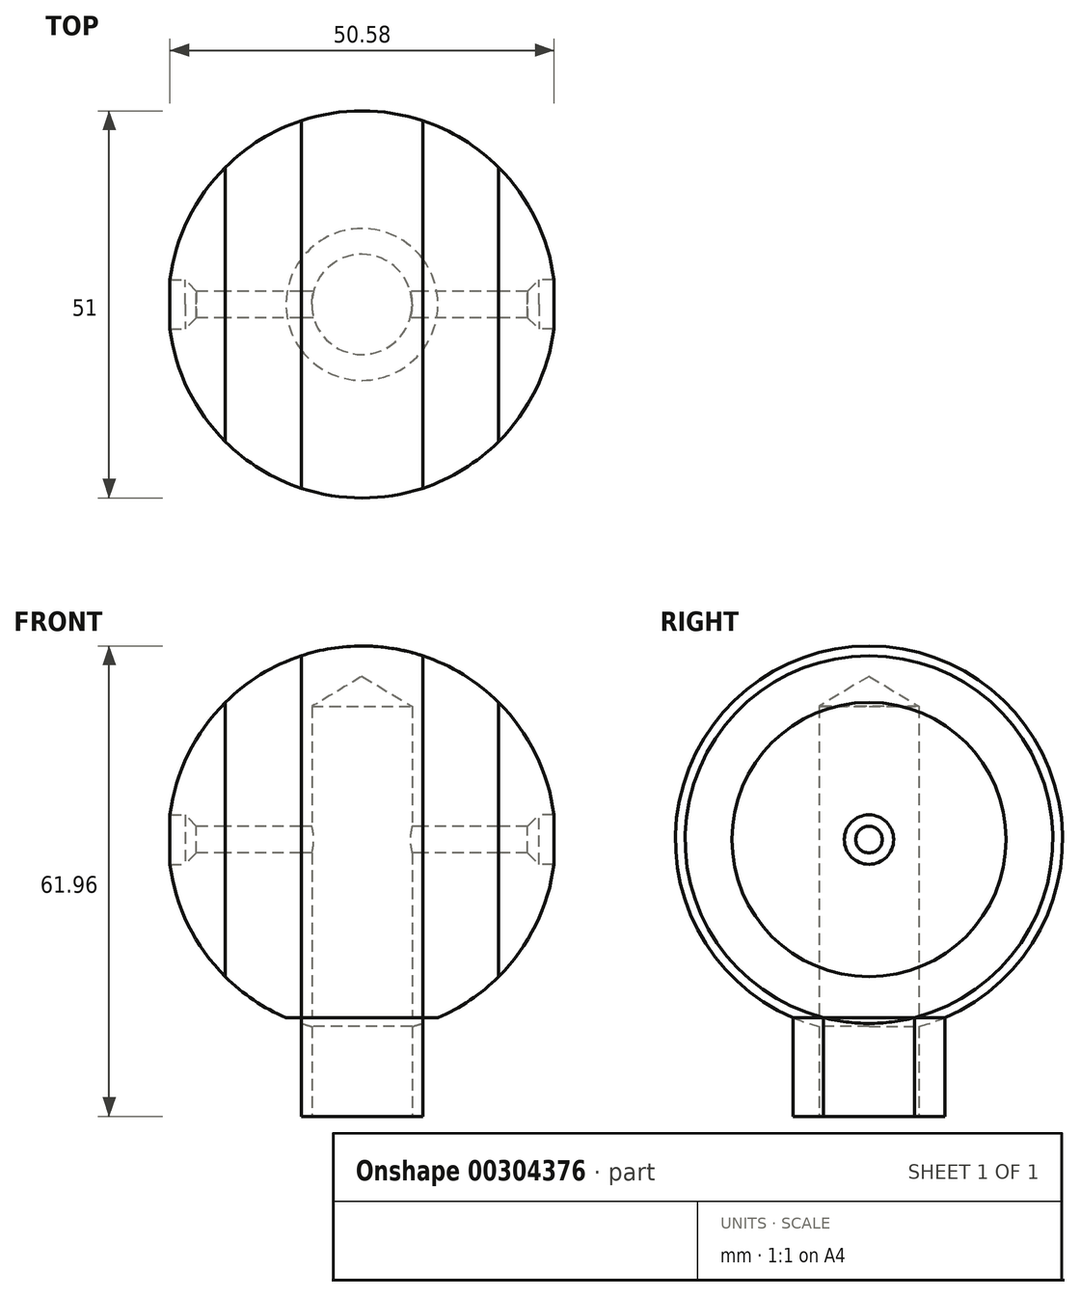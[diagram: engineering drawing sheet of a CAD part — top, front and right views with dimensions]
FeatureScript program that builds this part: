
annotation { "Feature Type Name" : "Feature", "Feature Type Description" : "" }
export const myFeature = defineFeature(function(context is Context, id is Id, definition is map)
    precondition{}
    {
        {
            assignVariable(context, id + "F0", {"name" : "ball_diameter", "anyValue" : 51});
        }
        {
            assignVariable(context, id + "F1", {"name" : "shaft_height", "anyValue" : 13});
        }
        {
            var Q0;
            Q0=qCreatedBy(makeId("Front.planeOp"),FACE);
            var sketch = newSketch(context, id + "F2", { "sketchPlane" : qUnion([Q0])});
            skCircle(sketch, "E0", {"center": v(0, 0) * mm, "radius": 25.5 * mm});
            skLineSegment(sketch, "E1.bottom", {"start": v(0, -23.46) * mm, "end": v(10, -23.46) * mm});
            skLineSegment(sketch, "E1.top", {"start": v(0, -36.46) * mm, "end": v(10, -36.46) * mm});
            skLineSegment(sketch, "E1.left", {"start": v(0, -23.46) * mm, "end": v(0, -36.46) * mm});
            skLineSegment(sketch, "E1.right", {"start": v(10, -23.46) * mm, "end": v(10, -36.46) * mm});
            skLineSegment(sketch, "E2", {"start": v(0, 44.91) * mm, "end": v(0, -49.6) * mm});
            skSolve(sketch);
        }
        {
            var Q0;
            {var subQ0=sQuery(id+"F2.wireOp",EDGE,"E1.bottom");Q0=makeQuery(id+"F2.imprint","IMPRINT",FACE,{"disambiguationData":[TD([[makeQuery(id+"F2.imprint","IMPRINT",EDGE,{"derivedFrom":subQ0}),1.0]])]});}
            var Q1;
            {var subQ4=sQuery(id+"F2.wireOp",EDGE,"E1.top");Q1=makeQuery(id+"F2.imprint","IMPRINT",FACE,{"disambiguationData":[TD([[makeQuery(id+"F2.imprint","IMPRINT",EDGE,{"derivedFrom":subQ4}),1.0]])]});}
            var Q2;
            Q2=sQuery(id+"F2.wireOp",EDGE,"E2");
            revolve(context, id + "F3", {"entities" : qUnion([Q0, Q1]), "axis" : qUnion([Q2]), "revolveType" : RevolveType.FULL});
        }
        {
            var Q0;
            Q0=makeQuery(id+"F3.opRevolve","SWEPT_FACE",FACE,{"disambiguationData":[OSD([sQuery(id+"F2.wireOp",EDGE,"E1.top")])]});
            var sketch = newSketch(context, id + "F4", { "sketchPlane" : qUnion([Q0])});
            skPoint(sketch, "E3", {"position": v(0, 0) * mm});
            skSolve(sketch);
        }
        {
            var Q0;
            Q0=sQuery(id+"F4.wireOp",VERTEX,"E3");
            var Q1;
            Q1=makeQuery(id+"F3.opRevolve","SWEPT_BODY",BODY,{"disambiguationData":[OSD([sQuery(id+"F2.wireOp",EDGE,"E0"),sQuery(id+"F2.wireOp",EDGE,"E1.top"),sQuery(id+"F2.wireOp",EDGE,"E1.right"),sQuery(id+"F2.wireOp",EDGE,"E2")])]});
            var Q2;
            Q2=makeQuery(id+"F3.opRevolve","SWEPT_BODY",BODY,{"disambiguationData":[OSD([sQuery(id+"F2.wireOp",EDGE,"E0"),sQuery(id+"F2.wireOp",EDGE,"E1.bottom"),sQuery(id+"F2.wireOp",EDGE,"E2")])]});
            hole(context, id + "F5", {"style" : HoleStyle.SIMPLE, "endStyle" : HoleEndStyle.BLIND, "standardTappedOrClearance" : lookupTablePath({ "fit" : "Normal", "standard" : "ISO", "size" : "M12", "type" : "Clearance" }), "standardBlindInLast" : lookupTablePath({ "fit" : "Standard", "standard" : "ISO", "size" : "M12", "type" : "Clearance" }), "holeDiameter" : 13.2 * mm, "holeDepth" : (getVariable(context, 'ball_diameter') + getVariable(context, 'shaft_height') - 10) * mm, "tappedDepth" : 12 * mm, "tapClearance" : 3, "locations" : qUnion([Q0]), "scope" : qUnion([Q1, Q2])});
        }
        {
            var Q0;
            Q0=qCreatedBy(makeId("Front.planeOp"),FACE);
            var sketch = newSketch(context, id + "F6", { "sketchPlane" : qUnion([Q0])});
            skLineSegment(sketch, "E4.bottom", {"start": v(8, 29.45) * mm, "end": v(18, 29.45) * mm});
            skLineSegment(sketch, "E4.top", {"start": v(8, -40.67) * mm, "end": v(18, -40.67) * mm});
            skLineSegment(sketch, "E4.left", {"start": v(8, 29.45) * mm, "end": v(8, -40.67) * mm});
            skLineSegment(sketch, "E4.right", {"start": v(18, 29.45) * mm, "end": v(18, -40.67) * mm});
            skLineSegment(sketch, "E5", {"start": v(0, 40) * mm, "end": v(0, -28.77) * mm});
            skLineSegment(sketch, "E6.MirrorCS", {"start": v(-8, 29.45) * mm, "end": v(-8, -40.67) * mm});
            skLineSegment(sketch, "E7.MirrorCS", {"start": v(-18, 29.45) * mm, "end": v(-18, -40.67) * mm});
            skLineSegment(sketch, "E8.MirrorCS", {"start": v(-8, 29.45) * mm, "end": v(-18, 29.45) * mm});
            skLineSegment(sketch, "E9.MirrorCS", {"start": v(-8, -40.67) * mm, "end": v(-18, -40.67) * mm});
            skSolve(sketch);
        }
        {
            var Q0;
            Q0=makeQuery(id+"F6.imprint","IMPRINT",FACE,{"disambiguationData":[TD([[makeQuery(id+"F6.imprint","IMPRINT",EDGE,{"derivedFrom":sQuery(id+"F6.wireOp",EDGE,"E4.bottom")}),-1.0]])]});
            var Q1;
            Q1=makeQuery(id+"F6.imprint","IMPRINT",FACE,{"disambiguationData":[TD([[makeQuery(id+"F6.imprint","IMPRINT",EDGE,{"derivedFrom":sQuery(id+"F6.wireOp",EDGE,"E6.MirrorCS")}),-1.0]])]});
            extrude(context, id + "F7", {"entities" : qUnion([Q0, Q1]), "endBound" : BoundingType.SYMMETRIC, "depth" : 50 * mm});
        }
        {
            var Q0;
            Q0=makeQuery(id+"F7.opExtrude","SWEPT_BODY",BODY,{"disambiguationData":[OSD([sQuery(id+"F6.wireOp",EDGE,"E4.bottom"),sQuery(id+"F6.wireOp",EDGE,"E4.top"),sQuery(id+"F6.wireOp",EDGE,"E4.left"),sQuery(id+"F6.wireOp",EDGE,"E4.right")])]});
            var Q1;
            Q1=makeQuery(id+"F3.opRevolve","SWEPT_BODY",BODY,{"disambiguationData":[OSD([sQuery(id+"F2.wireOp",EDGE,"E0"),sQuery(id+"F2.wireOp",EDGE,"E1.bottom"),sQuery(id+"F2.wireOp",EDGE,"E2")])]});
            var Q2;
            Q2=makeQuery(id+"F3.opRevolve","SWEPT_BODY",BODY,{"disambiguationData":[OSD([sQuery(id+"F2.wireOp",EDGE,"E0"),sQuery(id+"F2.wireOp",EDGE,"E1.bottom"),sQuery(id+"F2.wireOp",EDGE,"E2")])]});
            booleanBodies(context, id + "F8", {"operationType" : BooleanOperationType.INTERSECTION, "tools" : qUnion([Q0, Q1]), "targets" : qUnion([Q2]), "keepTools" : true});
        }
        {
            var Q0;
            Q0=makeQuery(id+"F3.opRevolve","SWEPT_BODY",BODY,{"disambiguationData":[OSD([sQuery(id+"F2.wireOp",EDGE,"E0"),sQuery(id+"F2.wireOp",EDGE,"E1.bottom"),sQuery(id+"F2.wireOp",EDGE,"E2")])]});
            var Q1;
            Q1=makeQuery(id+"F7.opExtrude","SWEPT_BODY",BODY,{"disambiguationData":[OSD([sQuery(id+"F6.wireOp",EDGE,"E6.MirrorCS"),sQuery(id+"F6.wireOp",EDGE,"E7.MirrorCS"),sQuery(id+"F6.wireOp",EDGE,"E8.MirrorCS"),sQuery(id+"F6.wireOp",EDGE,"E9.MirrorCS")])]});
            booleanBodies(context, id + "F9", {"operationType" : BooleanOperationType.INTERSECTION, "tools" : qUnion([Q0, Q1]), "keepTools" : true});
        }
        {
            var Q0;
            Q0=makeQuery(id+"F7.opExtrude","SWEPT_BODY",BODY,{"disambiguationData":[OSD([sQuery(id+"F6.wireOp",EDGE,"E6.MirrorCS"),sQuery(id+"F6.wireOp",EDGE,"E7.MirrorCS"),sQuery(id+"F6.wireOp",EDGE,"E8.MirrorCS"),sQuery(id+"F6.wireOp",EDGE,"E9.MirrorCS")])]});
            var Q1;
            Q1=makeQuery(id+"F7.opExtrude","SWEPT_BODY",BODY,{"disambiguationData":[OSD([sQuery(id+"F6.wireOp",EDGE,"E4.bottom"),sQuery(id+"F6.wireOp",EDGE,"E4.top"),sQuery(id+"F6.wireOp",EDGE,"E4.left"),sQuery(id+"F6.wireOp",EDGE,"E4.right")])]});
            var Q2;
            Q2=makeQuery(id+"F3.opRevolve","SWEPT_BODY",BODY,{"disambiguationData":[OSD([sQuery(id+"F2.wireOp",EDGE,"E0"),sQuery(id+"F2.wireOp",EDGE,"E1.bottom"),sQuery(id+"F2.wireOp",EDGE,"E2")])]});
            var Q3;
            Q3=makeQuery(id+"F3.opRevolve","SWEPT_BODY",BODY,{"disambiguationData":[OSD([sQuery(id+"F2.wireOp",EDGE,"E0"),sQuery(id+"F2.wireOp",EDGE,"E1.top"),sQuery(id+"F2.wireOp",EDGE,"E1.right"),sQuery(id+"F2.wireOp",EDGE,"E2")])]});
            booleanBodies(context, id + "F10", {"operationType" : BooleanOperationType.SUBTRACTION, "tools" : qUnion([Q0, Q1]), "targets" : qUnion([Q2, Q3])});
        }
        {
            var Q0;
            Q0=qCreatedBy(makeId("Right.planeOp"),FACE);
            var sketch = newSketch(context, id + "F11", { "sketchPlane" : qUnion([Q0])});
            skCircle(sketch, "E10", {"center": v(0, 0) * mm, "radius": 1.75 * mm});
            skCircle(sketch, "E11", {"center": v(0, 0) * mm, "radius": 3.25 * mm});
            skSolve(sketch);
        }
        {
            var Q0;
            Q0=makeQuery(id+"F11.imprint","IMPRINT",FACE,{"disambiguationData":[TD([[makeQuery(id+"F11.imprint","IMPRINT",EDGE,{"derivedFrom":sQuery(id+"F11.wireOp",EDGE,"E10")}),1.0]])]});
            extrude(context, id + "F12", {"entities" : qUnion([Q0]), "operationType" : NewBodyOperationType.REMOVE, "endBound" : BoundingType.SYMMETRIC, "depth" : 70 * mm});
        }
        {
            var Q0;
            Q0=qCreatedBy(makeId("Right.planeOp"),FACE);
            cPlane(context, id + "F13", {"entities" : qUnion([Q0]), "cplaneType" : CPlaneType.OFFSET, "offset" : 23.5 * mm, "width" : 150 * mm, "height" : 150 * mm});
        }
        {
            var Q0;
            Q0=qCreatedBy(id+"F13.planeOp",FACE);
            var sketch = newSketch(context, id + "F14", { "sketchPlane" : qUnion([Q0])});
            skCircle(sketch, "E12", {"center": v(0, 0) * mm, "radius": 3.25 * mm});
            skSolve(sketch);
        }
        {
            var Q0;
            Q0 = qSketchRegion(id + "F14", true);
            extrude(context, id + "F15", {"entities" : qUnion([Q0]), "operationType" : NewBodyOperationType.REMOVE, "depth" : 25 * mm});
        }
        {
            var Q0;
            Q0=makeQuery(id+"F15.boolean.opBoolean","INTERSECT",EDGE,{"derivedFrom":[makeQuery(id+"F12.boolean.opBoolean","COPY",FACE,{"disambiguationData":[TD([makeQuery(id+"F10.opBoolean","COPY",FACE,{"derivedFrom":makeQuery(id+"F7.opExtrude","SWEPT_FACE",FACE,{"disambiguationData":[OSD([sQuery(id+"F6.wireOp",EDGE,"E4.right")])]})})])],"derivedFrom":makeQuery(id+"F12.opExtrude","SWEPT_FACE",FACE,{"disambiguationData":[OSD([sQuery(id+"F11.wireOp",EDGE,"E10")])]})}),makeQuery(id+"F15.opExtrude","CAP_FACE",FACE,{"disambiguationData":[OSD([sQuery(id+"F14.wireOp",EDGE,"E12")])],"isStart":true})]});
            chamfer(context, id + "F16", {"entities" : qUnion([Q0]), "width" : 1.7 * mm, "tangentPropagation" : true});
        }
        {
            var Q0;
            Q0=qCreatedBy(makeId("Right.planeOp"),FACE);
            cPlane(context, id + "F17", {"entities" : qUnion([Q0]), "cplaneType" : CPlaneType.OFFSET, "offset" : 23.5 * mm, "oppositeDirection" : true, "width" : 150 * mm, "height" : 150 * mm});
        }
        {
            var Q0;
            Q0=qCreatedBy(id+"F17.planeOp",FACE);
            var sketch = newSketch(context, id + "F18", { "sketchPlane" : qUnion([Q0])});
            skCircle(sketch, "E13", {"center": v(0, 0) * mm, "radius": 3.25 * mm});
            skSolve(sketch);
        }
        {
            var Q0;
            Q0=makeQuery(id+"F18.imprint","IMPRINT",FACE,{"disambiguationData":[TD([[makeQuery(id+"F18.imprint","IMPRINT",EDGE,{"derivedFrom":sQuery(id+"F18.wireOp",EDGE,"E13")}),1.0]])]});
            var Q1;
            Q1=sQuery(id+"F18.wireOp",EDGE,"E13");
            extrude(context, id + "F19", {"entities" : qUnion([Q0]), "operationType" : NewBodyOperationType.REMOVE, "surfaceEntities" : qUnion([Q1]), "oppositeDirection" : true, "depth" : 25 * mm});
        }
        {
            var Q0;
            Q0=makeQuery(id+"F19.boolean.opBoolean","INTERSECT",EDGE,{"derivedFrom":[makeQuery(id+"F12.boolean.opBoolean","COPY",FACE,{"disambiguationData":[TD([makeQuery(id+"F10.opBoolean","COPY",FACE,{"derivedFrom":makeQuery(id+"F7.opExtrude","SWEPT_FACE",FACE,{"disambiguationData":[OSD([sQuery(id+"F6.wireOp",EDGE,"E7.MirrorCS")])]})})])],"derivedFrom":makeQuery(id+"F12.opExtrude","SWEPT_FACE",FACE,{"disambiguationData":[OSD([sQuery(id+"F11.wireOp",EDGE,"E10")])]})}),makeQuery(id+"F19.opExtrude","CAP_FACE",FACE,{"disambiguationData":[OSD([sQuery(id+"F18.wireOp",EDGE,"E13")])],"isStart":true})]});
            chamfer(context, id + "F20", {"entities" : qUnion([Q0]), "width" : 1.7 * mm, "tangentPropagation" : true});
        }
    });
